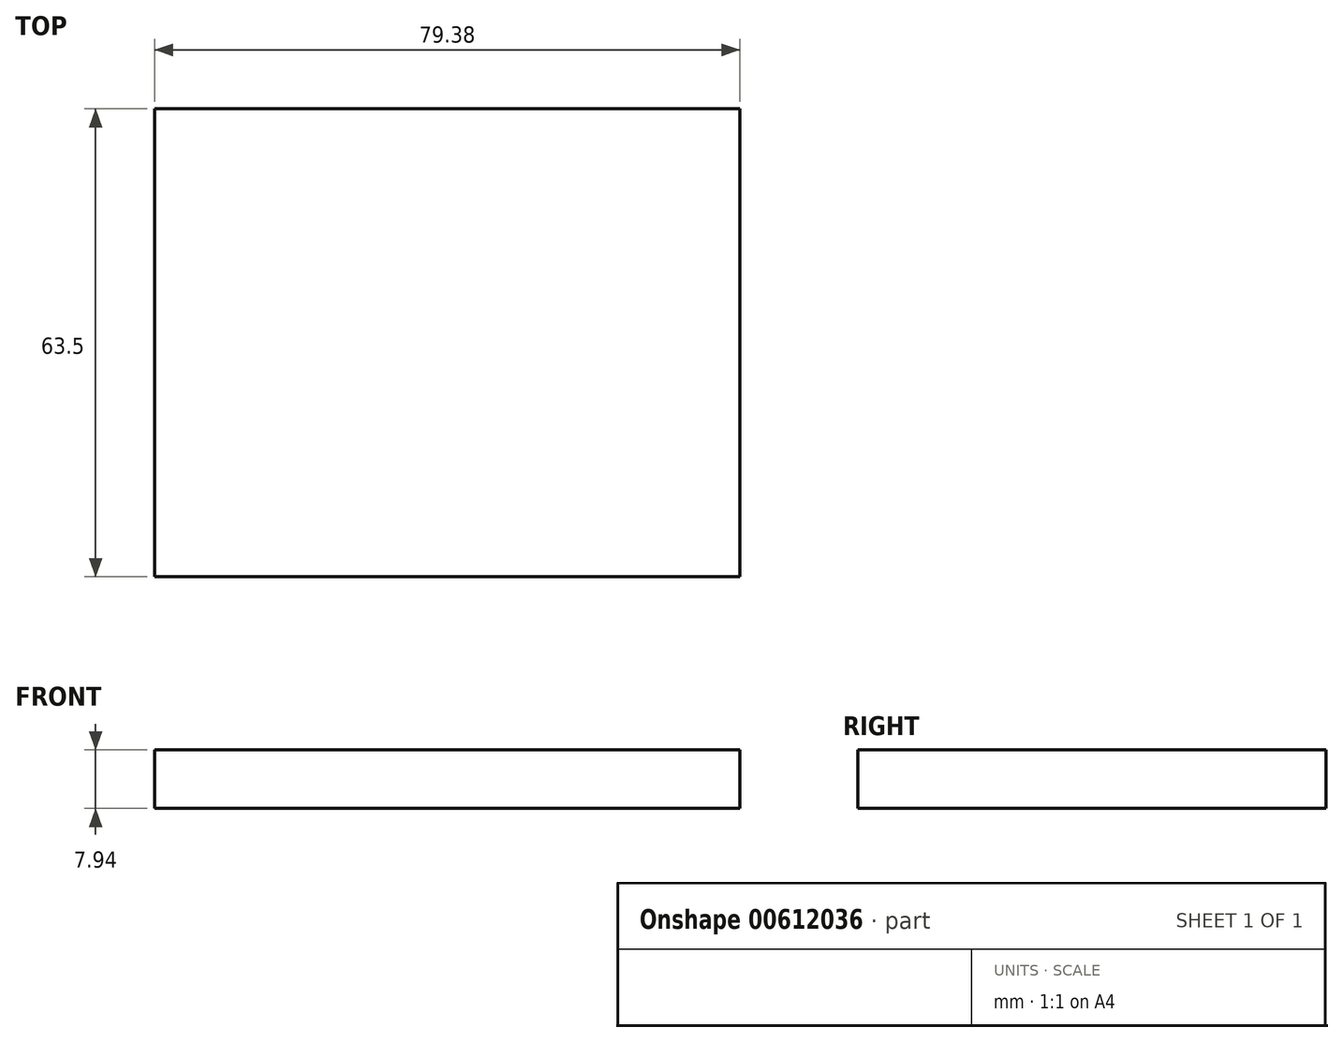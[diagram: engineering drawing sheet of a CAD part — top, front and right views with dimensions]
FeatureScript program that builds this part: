
annotation { "Feature Type Name" : "Feature", "Feature Type Description" : "" }
export const myFeature = defineFeature(function(context is Context, id is Id, definition is map)
    precondition{}
    {
        {
            var Q0;
            Q0=qCreatedBy(makeId("Top.planeOp"),FACE);
            var sketch = newSketch(context, id + "F0", { "sketchPlane" : qUnion([Q0])});
            skLineSegment(sketch, "E0", {"start": v(-31.18, 43.32) * mm, "end": v(48.2, 43.32) * mm});
            skLineSegment(sketch, "E1", {"start": v(48.2, 43.32) * mm, "end": v(48.2, -20.18) * mm});
            skLineSegment(sketch, "E2", {"start": v(48.2, -20.18) * mm, "end": v(-31.18, -20.18) * mm});
            skLineSegment(sketch, "E3", {"start": v(-31.18, -20.18) * mm, "end": v(-31.18, 43.32) * mm});
            skSolve(sketch);
        }
        {
            var Q0;
            Q0 = qSketchRegion(id + "F0", true);
            extrude(context, id + "F1", {"entities" : qUnion([Q0]), "depth" : 7.94 * mm, "offsetDistance" : 25.4 * mm});
        }
    });
